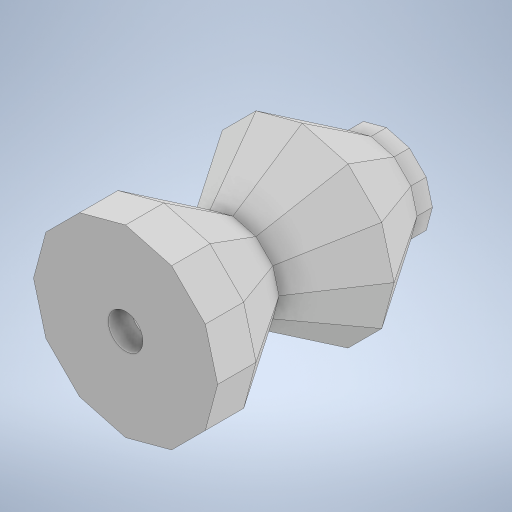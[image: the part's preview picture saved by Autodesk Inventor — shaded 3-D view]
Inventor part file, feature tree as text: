
AUTODESK INVENTOR PART (.ipt)
format: ipt  version: 2023 (Build 270158000, 158)  size: 354,304 bytes
history: native  units: in
note: dims shown in document units (in); Inventor stores cm internally (conversion verified against a paired STEP export)
features: sketch x6, extrude x4, projected_geometry x3, other x2, mirror x2, loft x1, shell x1
ambient origin geometry x8: Origin, YZ Plane, XZ Plane, XY Plane, X Axis, Y Axis, Z Axis, Center Point
bodies: Body1 (feature_tree)
feature tree (19):
  other  "솔리드1"
  sketch  "스케치1"
  other  "작업 평면1"
  loft  "로프트1"
  mirror  "미러1"
  mirror  "미러2"
  extrude  "돌출1"  Depth=0.3543in
  shell  "쉘2"  Thickness=0.4724in
  extrude  "돌출5"  TaperAngle=0.0deg  [1 undecoded]
  extrude  "돌출6"  TaperAngle=0.0deg  [1 undecoded]
  extrude  "돌출7"  Depth=0.1063in TaperAngle=0.0deg
  sketch  "스케치2"
  sketch  "스케치3"
  projected_geometry  "투영된 루프1"
  sketch  "스케치7"
  projected_geometry  "투영된 루프4"
  sketch  "스케치8"
  sketch  "스케치9"
  projected_geometry  "투영된 루프5"
note: 2 required parameter values undecoded (feature->parameter linkage not recoverable at this tier; creation-order binding heuristic only, values carry confidence <= 0.55)
